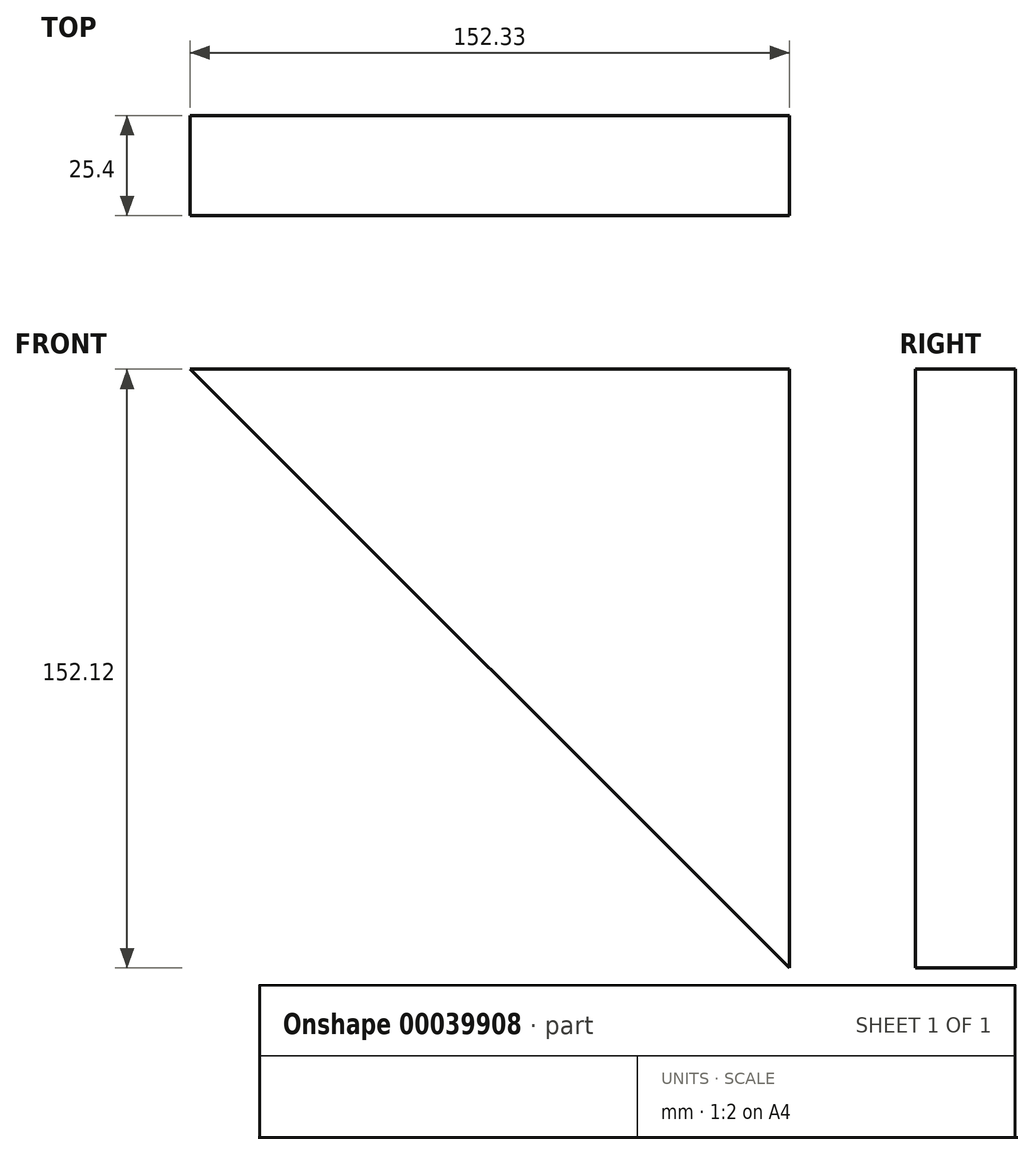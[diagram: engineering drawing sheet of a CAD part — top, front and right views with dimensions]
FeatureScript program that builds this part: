
annotation { "Feature Type Name" : "Feature", "Feature Type Description" : "" }
export const myFeature = defineFeature(function(context is Context, id is Id, definition is map)
    precondition{}
    {
        {
            var Q0;
            Q0=qCreatedBy(makeId("Front.planeOp"),FACE);
            var sketch = newSketch(context, id + "F0", { "sketchPlane" : qUnion([Q0])});
            skLineSegment(sketch, "E0", {"start": v(-76.06, 76.38) * mm, "end": v(76.27, -75.74) * mm});
            skLineSegment(sketch, "E1", {"start": v(76.27, -75.74) * mm, "end": v(76.27, 76.38) * mm});
            skLineSegment(sketch, "E2", {"start": v(76.27, 76.38) * mm, "end": v(-76.06, 76.38) * mm});
            skSolve(sketch);
        }
        {
            var Q0;
            Q0=makeQuery(id+"F0.imprint","IMPRINT",FACE,{"disambiguationData":[TD([[makeQuery(id+"F0.imprint","IMPRINT",EDGE,{"derivedFrom":sQuery(id+"F0.wireOp",EDGE,"E0")}),1.0]])]});
            extrude(context, id + "F1", {"entities" : qUnion([Q0]), "depth" : 25.4 * mm});
        }
    });
